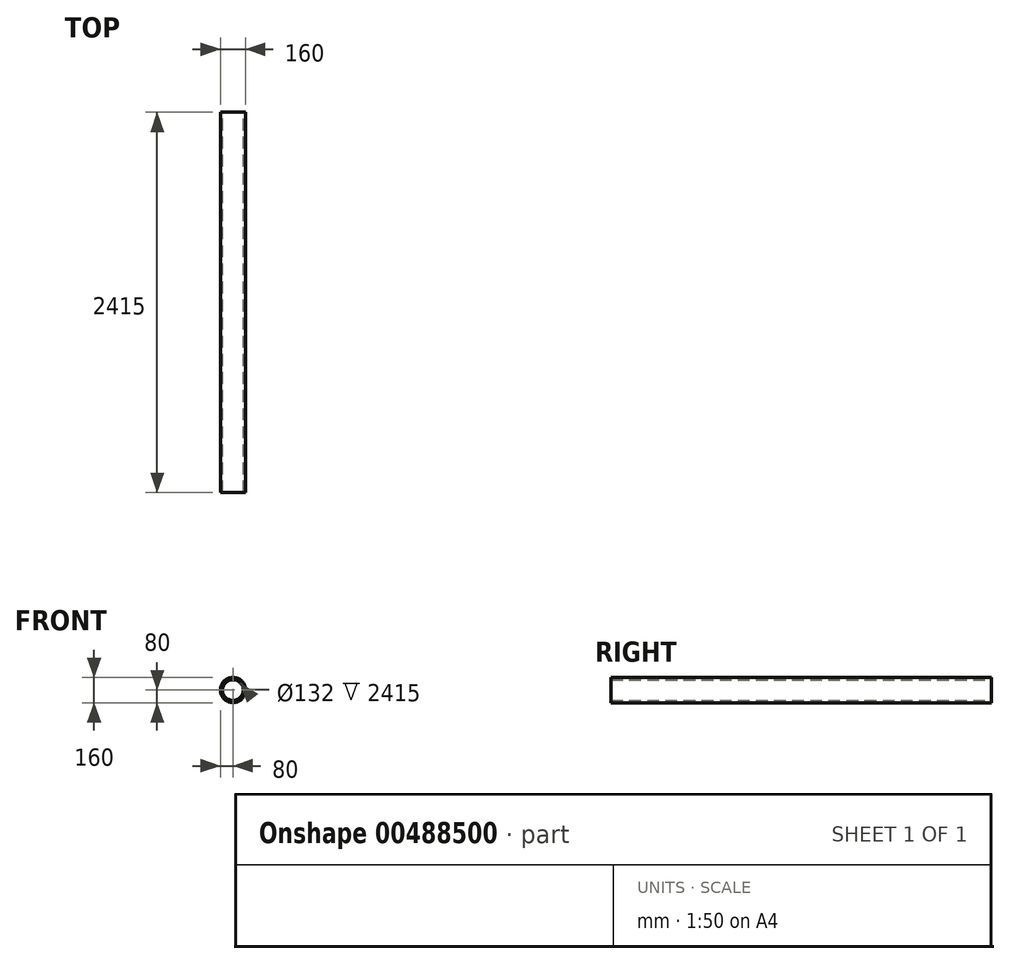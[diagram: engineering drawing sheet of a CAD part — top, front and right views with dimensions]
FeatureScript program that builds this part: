
annotation { "Feature Type Name" : "Feature", "Feature Type Description" : "" }
export const myFeature = defineFeature(function(context is Context, id is Id, definition is map)
    precondition{}
    {
        {
            var Q0;
            Q0=qCreatedBy(makeId("Front.planeOp"),FACE);
            var sketch = newSketch(context, id + "F0", { "sketchPlane" : qUnion([Q0])});
            skCircle(sketch, "E0", {"center": v(0, 0) * mm, "radius": 80 * mm});
            skCircle(sketch, "E1", {"center": v(0, 0) * mm, "radius": 66 * mm});
            skSolve(sketch);
        }
        {
            var Q0;
            Q0 = qSketchRegion(id + "F0", true);
            extrude(context, id + "F1", {"entities" : qUnion([Q0]), "depth" : 2415 * mm});
        }
    });
